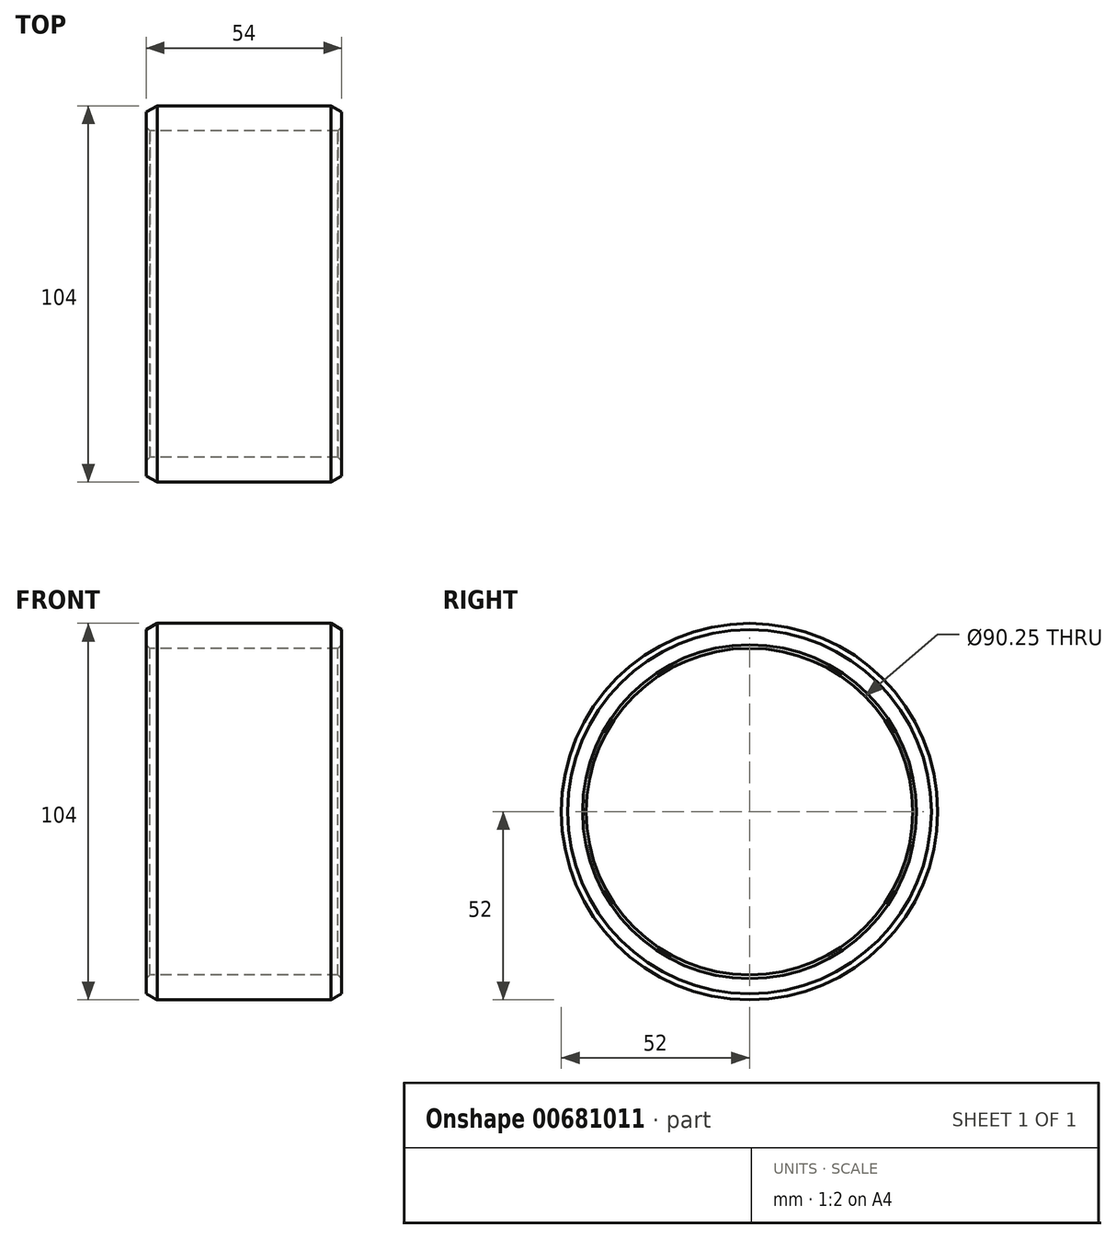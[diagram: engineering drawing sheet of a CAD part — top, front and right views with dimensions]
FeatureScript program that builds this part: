
annotation { "Feature Type Name" : "Feature", "Feature Type Description" : "" }
export const myFeature = defineFeature(function(context is Context, id is Id, definition is map)
    precondition{}
    {
        {
            var Q0;
            Q0=qCreatedBy(makeId("Right.planeOp"),FACE);
            var sketch = newSketch(context, id + "F0", { "sketchPlane" : qUnion([Q0])});
            skCircle(sketch, "E0", {"center": v(0, 0) * mm, "radius": 45.12 * mm});
            skCircle(sketch, "E1", {"center": v(0, 0) * mm, "radius": 52 * mm});
            skSolve(sketch);
        }
        {
            var Q0;
            Q0 = qSketchRegion(id + "F0", true);
            extrude(context, id + "F1", {"entities" : qUnion([Q0]), "endBound" : BoundingType.SYMMETRIC, "depth" : 54 * mm, "offsetDistance" : 25 * mm});
        }
        {
            var Q0;
            Q0=makeQuery(id+"F1.opExtrude","CAP_EDGE",EDGE,{"disambiguationData":[OSD([sQuery(id+"F0.wireOp",EDGE,"E0")])],"isStart":false});
            var Q1;
            Q1=makeQuery(id+"F1.opExtrude","CAP_EDGE",EDGE,{"disambiguationData":[OSD([sQuery(id+"F0.wireOp",EDGE,"E0")])],"isStart":true});
            chamfer(context, id + "F2", {"entities" : qUnion([Q0, Q1]), "width" : 1 * mm, "tangentPropagation" : true});
        }
        {
            var Q0;
            Q0=makeQuery(id+"F1.opExtrude","CAP_EDGE",EDGE,{"disambiguationData":[OSD([sQuery(id+"F0.wireOp",EDGE,"E1")])],"isStart":true});
            var Q1;
            Q1=makeQuery(id+"F1.opExtrude","CAP_EDGE",EDGE,{"disambiguationData":[OSD([sQuery(id+"F0.wireOp",EDGE,"E1")])],"isStart":false});
            chamfer(context, id + "F3", {"entities" : qUnion([Q0, Q1]), "chamferType" : ChamferType.OFFSET_ANGLE, "width" : 3 * mm, "oppositeDirection" : false, "angle" : 30 * degree, "tangentPropagation" : true});
        }
    });
